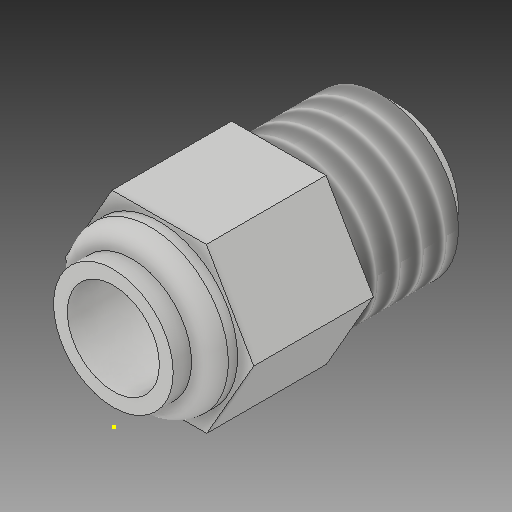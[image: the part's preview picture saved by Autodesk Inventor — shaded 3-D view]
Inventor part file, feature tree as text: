
AUTODESK INVENTOR PART (.ipt)
format: ipt  version: 2017 (Build 210142000, 142)  size: 180,736 bytes
history: native  units: mm
features: sketch x6, other x3
ambient origin geometry x8: Origin, YZ Plane, XZ Plane, XY Plane, X Axis, Y Axis, Z Axis, Center Point
bodies: Solid1 (feature_tree)
feature tree (9):
  other  "Pushfit-Adapter_MIR.ipt"
  other  "Solid1::Pushfit-Adapter_MIR.ipt"
  other  "TaggingFeature1"
  sketch  "Sketch1"  dims[d0=10.0mm]
  sketch  "Sketch2"
  sketch  "Sketch3"
  sketch  "Sketch4"
  sketch  "Sketch5"
  sketch  "Sketch6"
